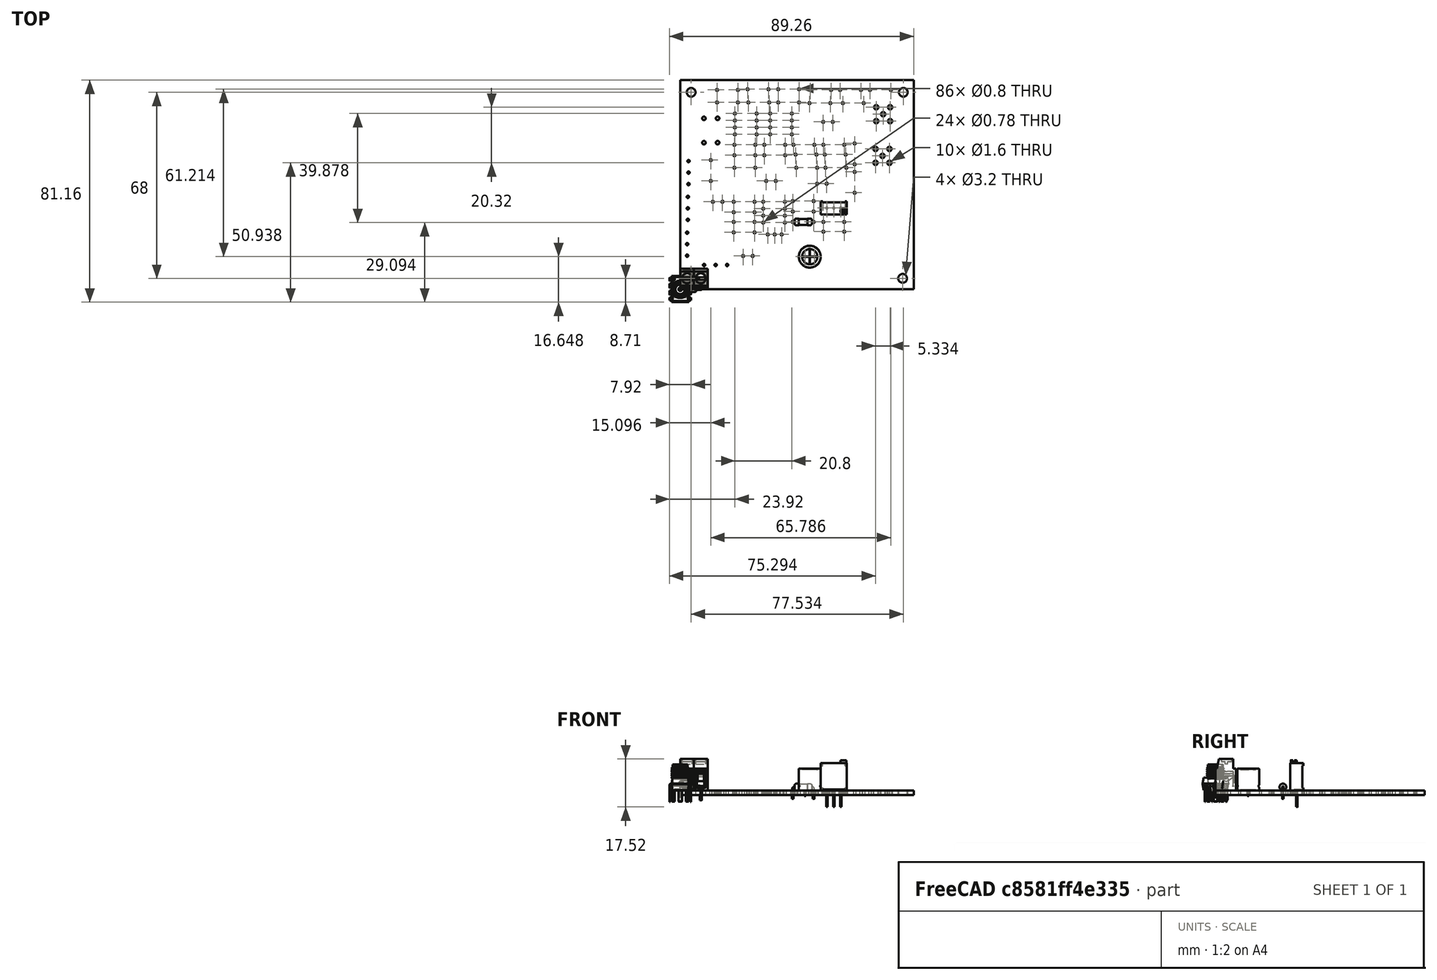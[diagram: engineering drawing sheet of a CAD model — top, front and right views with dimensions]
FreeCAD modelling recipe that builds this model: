
FCSTD DOCUMENT  (FreeCAD 0.19R24267 +148 (Git))
Label: Timebase
License: All rights reserved
LicenseURL: http://en.wikipedia.org/wiki/All_rights_reserved
objects: App::Link×44, Part::Feature×30, App::Part×8, Sketcher::SketchObject×2, PartDesign::CoordinateSystem×1
note: 33 computed .brp shape members not serialized (recipe doc carries the construction recipe); baked Part::Feature solids carry a one-line shape summary decoded from their .brp

FEATURE [Sketcher::SketchObject] PCB_Sketch_draft
  FullyConstrained = false
  sketch-geometry (4):
    g0: LineSegment StartX=0 StartY=76.454 StartZ=0 EndX=85.344 EndY=76.454 EndZ=0
    g1: LineSegment StartX=85.344 StartY=76.454 StartZ=0 EndX=85.344 EndY=0 EndZ=0
    g2: LineSegment StartX=85.344 StartY=0 StartZ=0 EndX=0 EndY=0 EndZ=0
    g3: LineSegment StartX=0 StartY=0 StartZ=0 EndX=0 EndY=76.454 EndZ=0
  constraints (4):
    c: Coincident(g2,g3)
    c: Coincident(g0,g3)
    c: Coincident(g1,g2)
    c: Coincident(g0,g1)
FEATURE [PartDesign::CoordinateSystem] Local_CS_758f
  AttacherType = Attacher::AttachEngine3D
FEATURE [Part::Feature] Pcb_758f
  Placement = pos=(-97.028,138.43,0) rot=(0,0,1;0rad)
  shape: bbox 85.34 x 76.45 x 1.6 mm, 146 faces (baked)
FEATURE [Sketcher::SketchObject] PCB_Sketch_758f
  FullyConstrained = false
  sketch-geometry (4):
    g0: LineSegment StartX=0 StartY=76.454 StartZ=0 EndX=85.344 EndY=76.454 EndZ=0
    g1: LineSegment StartX=85.344 StartY=76.454 StartZ=0 EndX=85.344 EndY=0 EndZ=0
    g2: LineSegment StartX=85.344 StartY=0 StartZ=0 EndX=0 EndY=0 EndZ=0
    g3: LineSegment StartX=0 StartY=0 StartZ=0 EndX=0 EndY=76.454 EndZ=0
  constraints (4):
    c: Coincident(g2,g3)
    c: Coincident(g0,g3)
    c: Coincident(g1,g2)
    c: Coincident(g0,g1)
FEATURE [Part::Feature] Shape  label="R426_R_Axial_DIN0207_L63mm_D25mm_P762mm_Horizontal_96b38c16849e"
  Placement = pos=(48.768,24.638,0) rot=(0,0,1;3.14159rad)
  shape: bbox 8.418 x 2.706 x 5.603 mm, 15 faces (baked)
FEATURE [Part::Feature] Part__Feature  label="D_DO-35_SOD27_P7.62mm_Horizontal"
  shape: bbox 8.244 x 0.5 x 4.312 mm, 7 faces (baked)
FEATURE [Part::Feature] Part__Feature001  label="D_DO-35_SOD27_P7.62mm_Horizontal001"
  shape: bbox 4 x 2.165 x 2.165 mm, 9 faces (baked)
FEATURE [App::Part] D_DO_35_SOD27_P7_62mm_Horizontal  label="D401_D_DO-35_SOD27_P7.62mm_Horizontal002_a58dadb01c92"
  Group = -> [Part__Feature,Part__Feature001]
  Origin = -> Origin008
  Placement = pos=(24.638,73.152,0) rot=(0,0,1;0rad)
FEATURE [App::Link] R426_R_Axial_DIN0207_L63mm_D25mm_P762mm_Horizontal_96b38c16849e_ln_  label="R411_R_Axial_DIN0207_L63mm_D25mm_P762mm_Horizontal_dd1791483003"
  LinkPlacement = pos=(13.462,68.326,0) rot=(0,0,1;0rad)
  LinkedObject = -> Shape
  Placement = pos=(13.462,68.326,0) rot=(0,0,1;0rad)
FEATURE [Part::Feature] Shape001  label="C405_CP_Radial_D80mm_P350mm_98bf3544fc31"
  Placement = pos=(45.5913,11.938,0) rot=(0,0,1;0rad)
  shape: bbox 9.886 x 10.23 x 10 mm, 54 faces (baked)
FEATURE [App::Link] R426_R_Axial_DIN0207_L63mm_D25mm_P762mm_Horizontal_96b38c16849e_ln_001  label="R425_R_Axial_DIN0207_L63mm_D25mm_P762mm_Horizontal_9357a432a3ac"
  LinkPlacement = pos=(52.324,24.638,0) rot=(0,0,1;0rad)
  LinkedObject = -> Shape
  Placement = pos=(52.324,24.638,0) rot=(0,0,1;0rad)
FEATURE [App::Link] R426_R_Axial_DIN0207_L63mm_D25mm_P762mm_Horizontal_96b38c16849e_ln_002  label="R417_R_Axial_DIN0207_L63mm_D25mm_P762mm_Horizontal_e48147e24a71"
  LinkPlacement = pos=(19.558,20.828,0) rot=(0,0,1;0rad)
  LinkedObject = -> Shape
  Placement = pos=(19.558,20.828,0) rot=(0,0,1;0rad)
FEATURE [App::Link] R426_R_Axial_DIN0207_L63mm_D25mm_P762mm_Horizontal_96b38c16849e_ln_003  label="R412_R_Axial_DIN0207_L63mm_D25mm_P762mm_Horizontal_5f7197d756d8"
  LinkPlacement = pos=(24.892,68.326,0) rot=(0,0,1;0rad)
  LinkedObject = -> Shape
  Placement = pos=(24.892,68.326,0) rot=(0,0,1;0rad)
FEATURE [App::Link] R426_R_Axial_DIN0207_L63mm_D25mm_P762mm_Horizontal_96b38c16849e_ln_004  label="R401_R_Axial_DIN0207_L63mm_D25mm_P762mm_Horizontal_f955ca19a62c"
  LinkPlacement = pos=(11.176,47.244,0) rot=(0,0,-1;1.5708rad)
  LinkedObject = -> Shape
  Placement = pos=(11.176,47.244,0) rot=(0,0,-1;1.5708rad)
FEATURE [App::Link] C405_CP_Radial_D80mm_P350mm_98bf3544fc31_ln_  label="C401_CP_Radial_D80mm_P350mm_d1dd1edc5a97"
  LinkPlacement = pos=(11.938,32.004,0) rot=(0,0,1;0rad)
  LinkedObject = -> Shape001
  Placement = pos=(11.938,32.004,0) rot=(0,0,1;0rad)
FEATURE [App::Link] D401_D_DO_35_SOD27_P7_62mm_Horizontal002_a58dadb01c92_ln_  label="D402_D_DO-35_SOD27_P7.62mm_Horizontal002_911bd0e35fae"
  LinkPlacement = pos=(43.434,73.152,0) rot=(0,0,1;3.14159rad)
  LinkedObject = -> D_DO_35_SOD27_P7_62mm_Horizontal
  Placement = pos=(43.434,73.152,0) rot=(0,0,1;3.14159rad)
FEATURE [App::Link] R426_R_Axial_DIN0207_L63mm_D25mm_P762mm_Horizontal_96b38c16849e_ln_005  label="R415_R_Axial_DIN0207_L63mm_D25mm_P762mm_Horizontal_2c18ec95c2a3"
  LinkPlacement = pos=(58.42,72.898,0) rot=(0,0,1;0rad)
  LinkedObject = -> Shape
  Placement = pos=(58.42,72.898,0) rot=(0,0,1;0rad)
FEATURE [App::Link] C405_CP_Radial_D80mm_P350mm_98bf3544fc31_ln_001  label="C403_CP_Radial_D80mm_P350mm_8a6e5d1b3050"
  LinkPlacement = pos=(34.9267,39.624,0) rot=(0,0,1;3.14159rad)
  LinkedObject = -> Shape001
  Placement = pos=(34.9267,39.624,0) rot=(0,0,1;3.14159rad)
FEATURE [App::Link] R426_R_Axial_DIN0207_L63mm_D25mm_P762mm_Horizontal_96b38c16849e_ln_006  label="R419_R_Axial_DIN0207_L63mm_D25mm_P762mm_Horizontal_3cb2f076483c"
  LinkPlacement = pos=(19.558,32.004,0) rot=(0,0,1;0rad)
  LinkedObject = -> Shape
  Placement = pos=(19.558,32.004,0) rot=(0,0,1;0rad)
FEATURE [Part::Feature] Part__Feature002  label="OPA347PA"
  Placement = pos=(0.013,0.081953,-0.39) rot=(1,0,0;1.5708rad)
  shape: bbox 0.762 x 1.461 x 6.731 mm, 18 faces (baked)
FEATURE [Part::Feature] Part__Feature003  label="OPA347PA001"
  Placement = pos=(0.013,0.081953,-0.39) rot=(1,0,0;1.5708rad)
  shape: bbox 0.762 x 0.9589 x 6.731 mm, 15 faces (baked)
FEATURE [Part::Feature] Part__Feature004  label="OPA347PA002"
  Placement = pos=(0.013,0.081953,-0.39) rot=(1,0,0;1.5708rad)
  shape: bbox 0.762 x 1.461 x 6.731 mm, 18 faces (baked)
FEATURE [Part::Feature] Part__Feature005  label="OPA347PA003"
  Placement = pos=(0.013,0.081953,-0.39) rot=(1,0,0;1.5708rad)
  shape: bbox 0.762 x 0.9589 x 6.731 mm, 15 faces (baked)
FEATURE [Part::Feature] Part__Feature006  label="OPA347PA004"
  Placement = pos=(0.013,0.081953,-0.39) rot=(1,0,0;1.5708rad)
  shape: bbox 0.762 x 1.461 x 6.731 mm, 18 faces (baked)
FEATURE [Part::Feature] Part__Feature007  label="OPA347PA005"
  Placement = pos=(0.013,0.081953,-0.39) rot=(1,0,0;1.5708rad)
  shape: bbox 0.762 x 0.9589 x 6.731 mm, 15 faces (baked)
FEATURE [Part::Feature] Part__Feature008  label="OPA347PA006"
  Placement = pos=(0.013,0.081953,-0.39) rot=(1,0,0;1.5708rad)
  shape: bbox 0.762 x 1.461 x 6.731 mm, 18 faces (baked)
FEATURE [Part::Feature] Part__Feature009  label="OPA347PA007"
  Placement = pos=(0.013,0.081953,-0.39) rot=(1,0,0;1.5708rad)
  shape: bbox 0.762 x 0.9589 x 6.731 mm, 15 faces (baked)
FEATURE [Part::Feature] Part__Feature010  label="OPA347PA008"
  Placement = pos=(0.013,0.081953,-0.39) rot=(1,0,0;1.5708rad)
  shape: bbox 6.35 x 9.589 x 4.572 mm, 17 faces (baked)
FEATURE [Part::Feature] Part__Feature011  label="OPA347PA009"
  Placement = pos=(0.013,0.081953,-0.39) rot=(1,0,0;1.5708rad)
  shape: bbox 0.6132 x 0.6132 x 0.508 mm, 4 faces (baked)
FEATURE [App::Part] OPA347PA010  label="U403_OPA347PA010_c6fd33d6b5eb"
  Group = -> [Part__Feature002,Part__Feature003,Part__Feature004,Part__Feature005,Part__Feature006,Part__Feature007,Part__Feature008,Part__Feature009,Part__Feature010,Part__Feature011]
  Origin = -> Origin009
  Placement = pos=(34.29,28.194,0) rot=(0,0,1;0rad)
FEATURE [App::Link] D401_D_DO_35_SOD27_P7_62mm_Horizontal002_a58dadb01c92_ln_001  label="D405_D_DO-35_SOD27_P7.62mm_Horizontal002_9d44dfe04af6"
  LinkPlacement = pos=(42.418,44.45,0) rot=(0,0,1;0rad)
  LinkedObject = -> D_DO_35_SOD27_P7_62mm_Horizontal
  Placement = pos=(42.418,44.45,0) rot=(0,0,1;0rad)
FEATURE [App::Link] R426_R_Axial_DIN0207_L63mm_D25mm_P762mm_Horizontal_96b38c16849e_ln_007  label="R416_R_Axial_DIN0207_L63mm_D25mm_P762mm_Horizontal_a3ec67ffc637"
  LinkPlacement = pos=(69.342,72.898,0) rot=(0,0,1;0rad)
  LinkedObject = -> Shape
  Placement = pos=(69.342,72.898,0) rot=(0,0,1;0rad)
FEATURE [App::Link] C405_CP_Radial_D80mm_P350mm_98bf3544fc31_ln_002  label="C406_CP_Radial_D80mm_P350mm_5d0f856a23b9"
  LinkPlacement = pos=(55.7547,61.214,0) rot=(0,0,1;3.14159rad)
  LinkedObject = -> Shape001
  Placement = pos=(55.7547,61.214,0) rot=(0,0,1;3.14159rad)
FEATURE [App::Link] R426_R_Axial_DIN0207_L63mm_D25mm_P762mm_Horizontal_96b38c16849e_ln_008  label="R414_R_Axial_DIN0207_L63mm_D25mm_P762mm_Horizontal_e16ba095c79a"
  LinkPlacement = pos=(47.498,72.898,0) rot=(0,0,1;0rad)
  LinkedObject = -> Shape
  Placement = pos=(47.498,72.898,0) rot=(0,0,1;0rad)
FEATURE [App::Link] R426_R_Axial_DIN0207_L63mm_D25mm_P762mm_Horizontal_96b38c16849e_ln_009  label="R403_R_Axial_DIN0207_L63mm_D25mm_P762mm_Horizontal_d589118723d7"
  LinkPlacement = pos=(38.354,49.022,0) rot=(0,0,1;3.14159rad)
  LinkedObject = -> Shape
  Placement = pos=(38.354,49.022,0) rot=(0,0,1;3.14159rad)
FEATURE [Part::Feature] Part__Feature012  label="73391-0060"
  Placement = pos=(0,9e-16,-9e-16) rot=(1,0,0;1.5708rad)
  shape: bbox 4.16 x 4.16 x 0.3 mm, 6 faces (baked)
FEATURE [Part::Feature] Part__Feature013  label="73391-0061"
  Placement = pos=(0,9e-16,-9e-16) rot=(1,0,0;1.5708rad)
  shape: bbox 1.254 x 0.5508 x 2.67 mm, 9 faces (baked)
FEATURE [Part::Feature] Part__Feature014  label="73391-0062"
  Placement = pos=(0,9e-16,-9e-16) rot=(1,0,0;1.5708rad)
  shape: bbox 1.254 x 0.5508 x 2.67 mm, 9 faces (baked)
FEATURE [Part::Feature] Part__Feature015  label="73391-0063"
  Placement = pos=(0,9e-16,-9e-16) rot=(1,0,0;1.5708rad)
  shape: bbox 6.358 x 7.341 x 13.63 mm, 83 faces (baked)
FEATURE [Part::Feature] Part__Feature016  label="73391-0064"
  Placement = pos=(0,9e-16,-9e-16) rot=(1,0,0;1.5708rad)
  shape: bbox 3.46 x 3.46 x 2.77 mm, 7 faces (baked)
FEATURE [App::Part] _3391_0065  label="J9_73391-0065_751de25d1e29"
  Group = -> [Part__Feature012,Part__Feature013,Part__Feature014,Part__Feature015,Part__Feature016]
  Origin = -> Origin010
  Placement = pos=(74.168,64.008,0) rot=(0,0,1;0rad)
FEATURE [App::Link] J9_73391_0065_751de25d1e29_ln_  label="J9_73391-0065_751de25d1e29[2]"
  LinkPlacement = pos=(74.168,64.008,0) rot=(0,0,1;0rad)
  LinkedObject = -> _3391_0065
  Placement = pos=(74.168,64.008,0) rot=(0,0,1;0rad)
FEATURE [App::Link] R426_R_Axial_DIN0207_L63mm_D25mm_P762mm_Horizontal_96b38c16849e_ln_010  label="R413_R_Axial_DIN0207_L63mm_D25mm_P762mm_Horizontal_7eeb8a3caef1"
  LinkPlacement = pos=(35.814,68.326,0) rot=(0,0,1;0rad)
  LinkedObject = -> Shape
  Placement = pos=(35.814,68.326,0) rot=(0,0,1;0rad)
FEATURE [App::Link] R426_R_Axial_DIN0207_L63mm_D25mm_P762mm_Horizontal_96b38c16849e_ln_011  label="R422_R_Axial_DIN0207_L63mm_D25mm_P762mm_Horizontal_5ecc24362076"
  LinkPlacement = pos=(19.558,24.638,0) rot=(0,0,1;0rad)
  LinkedObject = -> Shape
  Placement = pos=(19.558,24.638,0) rot=(0,0,1;0rad)
FEATURE [App::Link] R426_R_Axial_DIN0207_L63mm_D25mm_P762mm_Horizontal_96b38c16849e_ln_012  label="R406_R_Axial_DIN0207_L63mm_D25mm_P762mm_Horizontal_069660b694ff"
  LinkPlacement = pos=(19.812,52.832,0) rot=(0,0,1;0rad)
  LinkedObject = -> Shape
  Placement = pos=(19.812,52.832,0) rot=(0,0,1;0rad)
FEATURE [App::Link] D401_D_DO_35_SOD27_P7_62mm_Horizontal002_a58dadb01c92_ln_002  label="D408_D_DO-35_SOD27_P7.62mm_Horizontal002_46fe6fc0bc71"
  LinkPlacement = pos=(59.436,68.072,0) rot=(0,0,1;0rad)
  LinkedObject = -> D_DO_35_SOD27_P7_62mm_Horizontal
  Placement = pos=(59.436,68.072,0) rot=(0,0,1;0rad)
FEATURE [App::Link] R426_R_Axial_DIN0207_L63mm_D25mm_P762mm_Horizontal_96b38c16849e_ln_013  label="R427_R_Axial_DIN0207_L63mm_D25mm_P762mm_Horizontal_7b5043e7ec34"
  LinkPlacement = pos=(52.324,21.082,0) rot=(0,0,1;0rad)
  LinkedObject = -> Shape
  Placement = pos=(52.324,21.082,0) rot=(0,0,1;0rad)
FEATURE [Part::Feature] Shape002  label="R424_Potentiometer_Bourns_3296W_Vertical_5014a80db3f9"
  Placement = pos=(58.684,29.718,0) rot=(0,0,1;0rad)
  shape: bbox 9.53 x 4.83 x 17.07 mm, 32 faces (baked)
FEATURE [App::Link] R426_R_Axial_DIN0207_L63mm_D25mm_P762mm_Horizontal_96b38c16849e_ln_014  label="R421_R_Axial_DIN0207_L63mm_D25mm_P762mm_Horizontal_8707e0924818"
  LinkPlacement = pos=(48.768,32.258,0) rot=(0,0,1;3.14159rad)
  LinkedObject = -> Shape
  Placement = pos=(48.768,32.258,0) rot=(0,0,1;3.14159rad)
FEATURE [App::Link] R426_R_Axial_DIN0207_L63mm_D25mm_P762mm_Horizontal_96b38c16849e_ln_015  label="R409_R_Axial_DIN0207_L63mm_D25mm_P762mm_Horizontal_5f0248fd6b37"
  LinkPlacement = pos=(52.324,52.832,0) rot=(0,0,1;0rad)
  LinkedObject = -> Shape
  Placement = pos=(52.324,52.832,0) rot=(0,0,1;0rad)
FEATURE [App::Link] R426_R_Axial_DIN0207_L63mm_D25mm_P762mm_Horizontal_96b38c16849e_ln_016  label="R428_R_Axial_DIN0207_L63mm_D25mm_P762mm_Horizontal_dfc8f80ca371"
  LinkPlacement = pos=(63.754,35.306,0) rot=(0,0,1;1.5708rad)
  LinkedObject = -> Shape
  Placement = pos=(63.754,35.306,0) rot=(0,0,1;1.5708rad)
FEATURE [App::Link] R426_R_Axial_DIN0207_L63mm_D25mm_P762mm_Horizontal_96b38c16849e_ln_017  label="R407_R_Axial_DIN0207_L63mm_D25mm_P762mm_Horizontal_5106d6ccafbb"
  LinkPlacement = pos=(30.734,52.832,0) rot=(0,0,1;0rad)
  LinkedObject = -> Shape
  Placement = pos=(30.734,52.832,0) rot=(0,0,1;0rad)
FEATURE [App::Link] D401_D_DO_35_SOD27_P7_62mm_Horizontal002_a58dadb01c92_ln_003  label="D406_D_DO-35_SOD27_P7.62mm_Horizontal002_cf8cdba62340"
  LinkPlacement = pos=(60.706,44.45,0) rot=(0,0,1;3.14159rad)
  LinkedObject = -> D_DO_35_SOD27_P7_62mm_Horizontal
  Placement = pos=(60.706,44.45,0) rot=(0,0,1;3.14159rad)
FEATURE [App::Link] J9_73391_0065_751de25d1e29_ln_001  label="J8_73391-0065_6ead0989832a"
  LinkPlacement = pos=(73.914,48.768,0) rot=(0,0,1;0rad)
  LinkedObject = -> _3391_0065
  Placement = pos=(73.914,48.768,0) rot=(0,0,1;0rad)
FEATURE [App::Link] R426_R_Axial_DIN0207_L63mm_D25mm_P762mm_Horizontal_96b38c16849e_ln_018  label="R405_R_Axial_DIN0207_L63mm_D25mm_P762mm_Horizontal_71255379b79a"
  LinkPlacement = pos=(13.462,72.898,0) rot=(0,0,1;0rad)
  LinkedObject = -> Shape
  Placement = pos=(13.462,72.898,0) rot=(0,0,1;0rad)
FEATURE [App::Link] U403_OPA347PA010_c6fd33d6b5eb_ln_  label="U401_OPA347PA010_2ab8ee650e3a"
  LinkPlacement = pos=(23.97,60.452,0) rot=(0,0,1;0rad)
  LinkedObject = -> OPA347PA010
  Placement = pos=(23.97,60.452,0) rot=(0,0,1;0rad)
FEATURE [App::Link] U403_OPA347PA010_c6fd33d6b5eb_ln_001  label="U401_OPA347PA010_2ab8ee650e3a[2]"
  LinkPlacement = pos=(23.97,60.452,0) rot=(0,0,1;0rad)
  LinkedObject = -> OPA347PA010
  Placement = pos=(23.97,60.452,0) rot=(0,0,1;0rad)
FEATURE [App::Link] R426_R_Axial_DIN0207_L63mm_D25mm_P762mm_Horizontal_96b38c16849e_ln_019  label="R423_R_Axial_DIN0207_L63mm_D25mm_P762mm_Horizontal_fe47b2319611"
  LinkPlacement = pos=(48.768,28.448,0) rot=(0,0,1;3.14159rad)
  LinkedObject = -> Shape
  Placement = pos=(48.768,28.448,0) rot=(0,0,1;3.14159rad)
FEATURE [Part::Feature] Part__Feature017  label="SOLID"
  shape: bbox 5.001 x 7.774 x 15.1 mm, 102 faces (baked)
FEATURE [Part::Feature] Part__Feature018  label="SOLID001"
  shape: bbox 5.001 x 7.774 x 15.1 mm, 102 faces (baked)
FEATURE [App::Part] _91137710002_1  label="J404_691137710002_1_aa849ba69819"
  Group = -> [Part__Feature017,Part__Feature018]
  Origin = -> Origin011
  Placement = pos=(16.176,66.484,0) rot=(0,0,1;3.14159rad)
FEATURE [App::Link] C405_CP_Radial_D80mm_P350mm_98bf3544fc31_ln_003  label="C404_CP_Radial_D80mm_P350mm_9f53755e8169"
  LinkPlacement = pos=(22.9853,12.192,0) rot=(0,0,1;0rad)
  LinkedObject = -> Shape001
  Placement = pos=(22.9853,12.192,0) rot=(0,0,1;0rad)
FEATURE [App::Link] D401_D_DO_35_SOD27_P7_62mm_Horizontal002_a58dadb01c92_ln_004  label="D403_D_DO-35_SOD27_P7.62mm_Horizontal002_2c64fccd57f6"
  LinkPlacement = pos=(52.832,49.276,0) rot=(0,0,1;0rad)
  LinkedObject = -> D_DO_35_SOD27_P7_62mm_Horizontal
  Placement = pos=(52.832,49.276,0) rot=(0,0,1;0rad)
FEATURE [App::Link] R426_R_Axial_DIN0207_L63mm_D25mm_P762mm_Horizontal_96b38c16849e_ln_020  label="R408_R_Axial_DIN0207_L63mm_D25mm_P762mm_Horizontal_61fd169c9d1a"
  LinkPlacement = pos=(49.022,52.832,0) rot=(0,0,1;3.14159rad)
  LinkedObject = -> Shape
  Placement = pos=(49.022,52.832,0) rot=(0,0,1;3.14159rad)
FEATURE [App::Link] J404_691137710002_1_aa849ba69819_ln_  label="J402_691137710002_1_e33a29fe56de"
  LinkPlacement = pos=(6.176,49.594,0) rot=(0,0,1;0rad)
  LinkedObject = -> _91137710002_1
  Placement = pos=(6.176,49.594,0) rot=(0,0,1;0rad)
FEATURE [App::Link] R426_R_Axial_DIN0207_L63mm_D25mm_P762mm_Horizontal_96b38c16849e_ln_021  label="R410_R_Axial_DIN0207_L63mm_D25mm_P762mm_Horizontal_3c69a267c242"
  LinkPlacement = pos=(63.754,53.34,0) rot=(0,0,-1;1.5708rad)
  LinkedObject = -> Shape
  Placement = pos=(63.754,53.34,0) rot=(0,0,-1;1.5708rad)
FEATURE [App::Link] R426_R_Axial_DIN0207_L63mm_D25mm_P762mm_Horizontal_96b38c16849e_ln_022  label="R404_R_Axial_DIN0207_L63mm_D25mm_P762mm_Horizontal_fed7218cdfd8"
  LinkPlacement = pos=(19.812,44.45,0) rot=(0,0,1;0rad)
  LinkedObject = -> Shape
  Placement = pos=(19.812,44.45,0) rot=(0,0,1;0rad)
FEATURE [App::Link] D401_D_DO_35_SOD27_P7_62mm_Horizontal002_a58dadb01c92_ln_005  label="D404_D_DO-35_SOD27_P7.62mm_Horizontal002_1b29f77ed16f"
  LinkPlacement = pos=(49.784,49.276,0) rot=(0,0,1;3.14159rad)
  LinkedObject = -> D_DO_35_SOD27_P7_62mm_Horizontal
  Placement = pos=(49.784,49.276,0) rot=(0,0,1;3.14159rad)
FEATURE [App::Link] C405_CP_Radial_D80mm_P350mm_98bf3544fc31_ln_004  label="C402_CP_Radial_D80mm_P350mm_13afafdb752a"
  LinkPlacement = pos=(53.538,38.608,0) rot=(0,0,1;3.14159rad)
  LinkedObject = -> Shape001
  Placement = pos=(53.538,38.608,0) rot=(0,0,1;3.14159rad)
FEATURE [App::Link] R426_R_Axial_DIN0207_L63mm_D25mm_P762mm_Horizontal_96b38c16849e_ln_023  label="R429_R_Axial_DIN0207_L63mm_D25mm_P762mm_Horizontal_513325376d6c"
  LinkPlacement = pos=(47.244,68.072,0) rot=(0,0,1;0rad)
  LinkedObject = -> Shape
  Placement = pos=(47.244,68.072,0) rot=(0,0,1;0rad)
FEATURE [App::Link] R426_R_Axial_DIN0207_L63mm_D25mm_P762mm_Horizontal_96b38c16849e_ln_024  label="R402_R_Axial_DIN0207_L63mm_D25mm_P762mm_Horizontal_47cc05b15c1c"
  LinkPlacement = pos=(19.812,49.022,0) rot=(0,0,1;0rad)
  LinkedObject = -> Shape
  Placement = pos=(19.812,49.022,0) rot=(0,0,1;0rad)
FEATURE [App::Link] U403_OPA347PA010_c6fd33d6b5eb_ln_002  label="U402_OPA347PA010_bf3c42dcce77"
  LinkPlacement = pos=(36.83,60.452,0) rot=(0,0,1;0rad)
  LinkedObject = -> OPA347PA010
  Placement = pos=(36.83,60.452,0) rot=(0,0,1;0rad)
FEATURE [App::Link] R424_Potentiometer_Bourns_3296W_Vertical_5014a80db3f9_ln_  label="R420_Potentiometer_Bourns_3296W_Vertical_7ce6f298ed42"
  LinkPlacement = pos=(37.094,20.066,0) rot=(0,0,1;0rad)
  LinkedObject = -> Shape002
  Placement = pos=(37.094,20.066,0) rot=(0,0,1;0rad)
FEATURE [App::Link] R426_R_Axial_DIN0207_L63mm_D25mm_P762mm_Horizontal_96b38c16849e_ln_025  label="R418_R_Axial_DIN0207_L63mm_D25mm_P762mm_Horizontal_928039f00f5f"
  LinkPlacement = pos=(19.558,28.194,0) rot=(0,0,1;0rad)
  LinkedObject = -> Shape
  Placement = pos=(19.558,28.194,0) rot=(0,0,1;0rad)
FEATURE [App::Part] Top_758f
  Group = -> [Shape,D_DO_35_SOD27_P7_62mm_Horizontal,R426_R_Axial_DIN0207_L63mm_D25mm_P762mm_Horizontal_96b38c16849e_ln_,Shape001,R426_R_Axial_DIN0207_L63mm_D25mm_P762mm_Horizontal_96b38c16849e_ln_001,R426_R_Axial_DIN0207_L63mm_D25mm_P762mm_Horizontal_96b38c16849e_ln_002,R426_R_Axial_DIN0207_L63mm_D25mm_P762mm_Horizontal_96b38c16849e_ln_003,R426_R_Axial_DIN0207_L63mm_D25mm_P762mm_Horizontal_96b38c16849e_ln_004,+43 more]
  Origin = -> Origin003
FEATURE [App::Part] Step_Models_758f
  Group = -> [Top_758f]
  Origin = -> Origin002
FEATURE [Part::Feature] pads_area057001  label="topPads_758f"
  Placement = pos=(-97.028,138.43,0.02) rot=(0,0,1;0rad)
  shape: bbox 76.29 x 65.99 x 2e-07 mm, 136 faces, 0 solids (baked)
FEATURE [Part::Feature] tracks_area001  label="topTracks_758f"
  Placement = pos=(-97.028,138.43,0.01) rot=(0,0,1;0rad)
  shape: bbox 74.14 x 64.19 x 2e-07 mm, 47 faces, 0 solids (baked)
FEATURE [Part::Feature] zones_area001  label="topZones_758f"
  Placement = pos=(-97.028,138.43,0.01) rot=(0,0,1;0rad)
  shape: bbox 84.58 x 75.69 x 2e-07 mm, 5 faces, 0 solids (baked)
FEATURE [Part::Feature] pads_area057059001  label="botPads_758f"
  Placement = pos=(-97.028,138.43,-1.62) rot=(0,0,1;0rad)
  shape: bbox 76.29 x 65.99 x 2e-07 mm, 136 faces, 0 solids (baked)
FEATURE [Part::Feature] tracks_area002001  label="botTracks_758f"
  Placement = pos=(-97.028,138.43,-1.61) rot=(0,0,1;0rad)
  shape: bbox 72.92 x 63.68 x 2e-07 mm, 35 faces, 0 solids (baked)
FEATURE [Part::Feature] zones_area002001  label="botZones_758f"
  Placement = pos=(-97.028,138.43,-1.61) rot=(0,0,1;0rad)
  shape: bbox 84.58 x 75.69 x 2e-07 mm, 5 faces, 0 solids (baked)
FEATURE [Part::Feature] topSilks_611a
  Placement = pos=(-97.028,138.43,0.07) rot=(0,0,1;0rad)
  shape: bbox 82.73 x 72.86 x 2e-07 mm, 393 faces, 0 solids (baked)
FEATURE [App::Part] Board_Geoms_758f
  Group = -> [Local_CS_758f,Pcb_758f,PCB_Sketch_758f,pads_area057001,tracks_area001,zones_area001,pads_area057059001,tracks_area002001,zones_area002001,topSilks_611a]
  Origin = -> Origin
FEATURE [App::Part] Board_758f  label="timebase"
  Group = -> [Board_Geoms_758f,Step_Models_758f]
  Origin = -> Origin001
